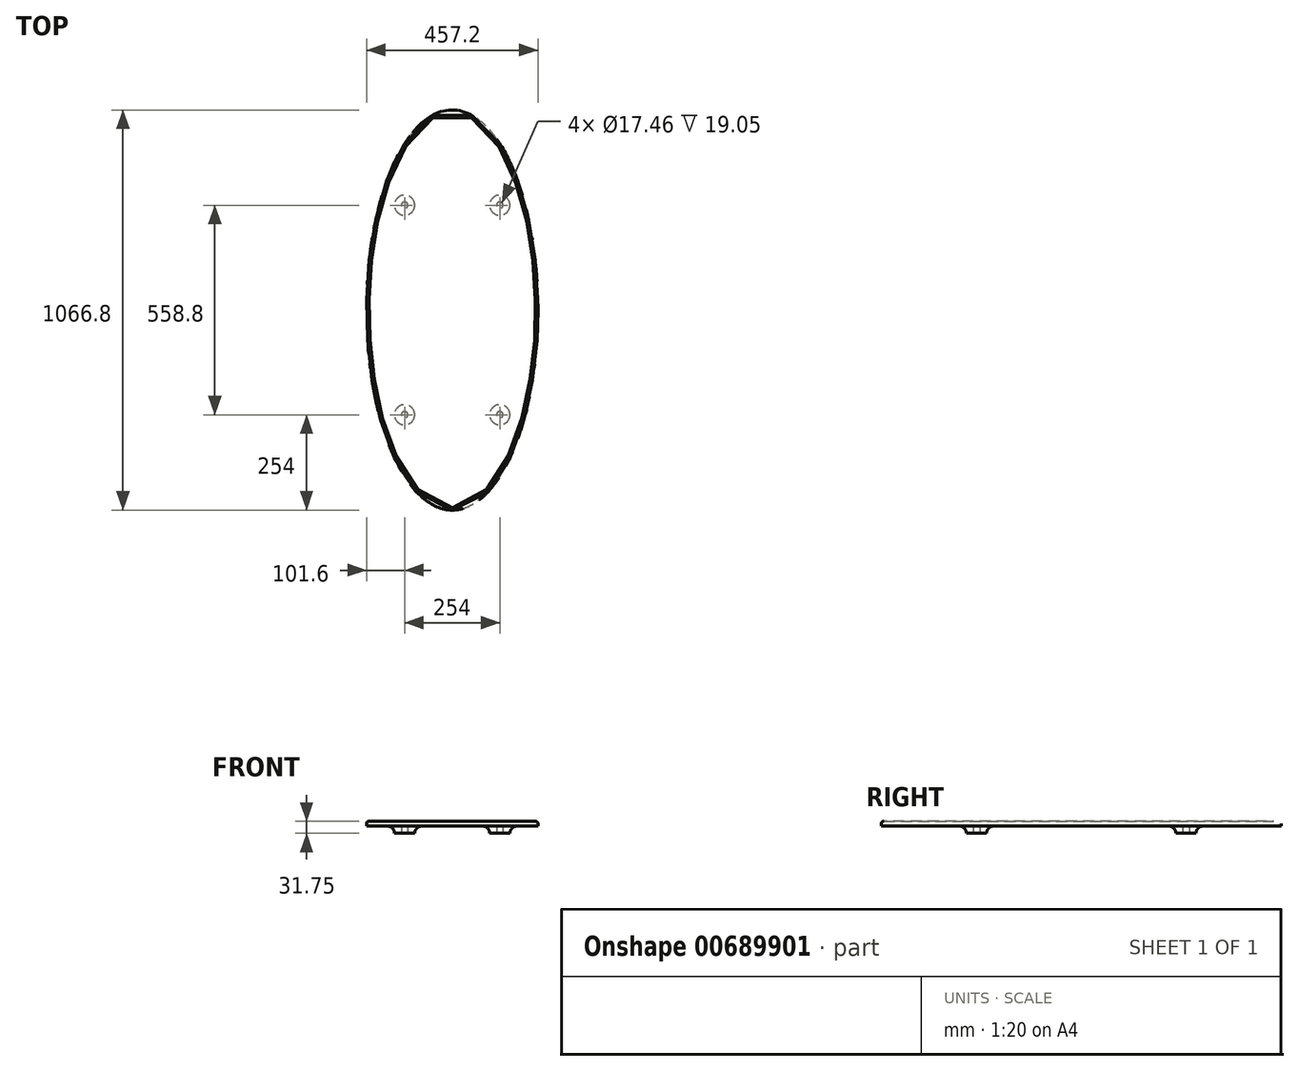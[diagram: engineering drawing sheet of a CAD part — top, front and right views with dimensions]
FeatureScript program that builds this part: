
annotation { "Feature Type Name" : "Feature", "Feature Type Description" : "" }
export const myFeature = defineFeature(function(context is Context, id is Id, definition is map)
    precondition{}
    {
        {
            var Q0;
            Q0=qCreatedBy(makeId("Top.planeOp"),FACE);
            var sketch = newSketch(context, id + "F0", { "sketchPlane" : qUnion([Q0])});
            skEllipse(sketch, "E0", {"center": v(0, 0) * mm, "majorRadius": 533.4 * mm, "minorRadius": 228.6 * mm, "majorAxis": v(0, -1)});
            skSolve(sketch);
        }
        {
            var Q0;
            Q0=makeQuery(id+"F0.imprint","IMPRINT",FACE,{"disambiguationData":[TD([[makeQuery(id+"F0.imprint","IMPRINT",EDGE,{"derivedFrom":sQuery(id+"F0.wireOp",EDGE,"E0")}),1.0]])]});
            extrude(context, id + "F1", {"entities" : qUnion([Q0]), "depth" : 31.75 * mm, "offsetDistance" : 25.4 * mm});
        }
        {
            var Q0;
            Q0=makeQuery(id+"F1.opExtrude","CAP_FACE",FACE,{"disambiguationData":[OSD([sQuery(id+"F0.wireOp",EDGE,"E0")])],"isStart":true});
            var sketch = newSketch(context, id + "F2", { "sketchPlane" : qUnion([Q0])});
            skLineSegment(sketch, "E1.bottom", {"start": v(-127, 279.4) * mm, "end": v(127, 279.4) * mm});
            skLineSegment(sketch, "E1.top", {"start": v(-127, -279.4) * mm, "end": v(127, -279.4) * mm});
            skLineSegment(sketch, "E1.left", {"start": v(-127, 279.4) * mm, "end": v(-127, -279.4) * mm});
            skLineSegment(sketch, "E1.right", {"start": v(127, 279.4) * mm, "end": v(127, -279.4) * mm});
            skPoint(sketch, "E1.middle", {"position": v(0, 0) * mm});
            skCircle(sketch, "E2", {"center": v(127, 279.4) * mm, "radius": 26.99 * mm});
            skCircle(sketch, "E3", {"center": v(-127, 279.4) * mm, "radius": 26.99 * mm});
            skCircle(sketch, "E4", {"center": v(-127, -279.4) * mm, "radius": 26.99 * mm});
            skCircle(sketch, "E5", {"center": v(127, -279.4) * mm, "radius": 26.99 * mm});
            skSolve(sketch);
        }
        {
            var Q0;
            Q0=makeQuery(id+"F2.imprint","IMPRINT",FACE,{"disambiguationData":[TD([[makeQuery(id+"F2.imprint","IMPRINT",EDGE,{"derivedFrom":makeQuery(id+"F1.opExtrude","CAP_EDGE",EDGE,{"disambiguationData":[OSD([sQuery(id+"F0.wireOp",EDGE,"E0")])],"isStart":true})}),-1.0]])]});
            var Q1;
            {var subQ5=sQuery(id+"F2.wireOp",EDGE,"E3");var subQ13=sQuery(id+"F2.wireOp",EDGE,"E1.bottom");var subQ14=makeQuery(id+"F2.imprint","INTERSECT",VERTEX,{"derivedFrom":[subQ13,subQ5]});Q1=makeQuery(id+"F2.imprint","IMPRINT",FACE,{"disambiguationData":[TD([[makeQuery(id+"F2.imprint","IMPRINT",EDGE,{"disambiguationData":[TD([[subQ14,-1.0]])],"derivedFrom":subQ13}),-1.0]])]});}
            extrude(context, id + "F3", {"entities" : qUnion([Q0, Q1]), "operationType" : NewBodyOperationType.REMOVE, "oppositeDirection" : true, "depth" : 19.05 * mm, "offsetDistance" : 25.4 * mm});
        }
        {
            var Q0;
            Q0=makeQuery(id+"F3.boolean.opBoolean","COPY",EDGE,{"derivedFrom":makeQuery(id+"F3.opExtrude","CAP_EDGE",EDGE,{"disambiguationData":[OSD([sQuery(id+"F2.wireOp",EDGE,"E2")])],"isStart":false})});
            var Q1;
            Q1=makeQuery(id+"F3.boolean.opBoolean","COPY",EDGE,{"derivedFrom":makeQuery(id+"F3.opExtrude","CAP_EDGE",EDGE,{"disambiguationData":[OSD([sQuery(id+"F2.wireOp",EDGE,"E3")])],"isStart":false})});
            var Q2;
            Q2=makeQuery(id+"F3.boolean.opBoolean","COPY",EDGE,{"derivedFrom":makeQuery(id+"F3.opExtrude","CAP_EDGE",EDGE,{"disambiguationData":[OSD([sQuery(id+"F2.wireOp",EDGE,"E5")])],"isStart":false})});
            var Q3;
            Q3=makeQuery(id+"F3.boolean.opBoolean","COPY",EDGE,{"derivedFrom":makeQuery(id+"F3.opExtrude","CAP_EDGE",EDGE,{"disambiguationData":[OSD([sQuery(id+"F2.wireOp",EDGE,"E4")])],"isStart":false})});
            fillet(context, id + "F4", {"entities" : qUnion([Q0, Q1, Q2, Q3]), "radius" : 19.05 * mm, "tangentPropagation" : true, "allowEdgeOverflow" : false});
        }
        {
            var Q0;
            Q0=makeQuery(id+"F1.opExtrude","CAP_EDGE",EDGE,{"disambiguationData":[OSD([sQuery(id+"F0.wireOp",EDGE,"E0")])],"isStart":false});
            var Q1;
            Q1=makeQuery(id+"F3.boolean.opBoolean","COPY",EDGE,{"derivedFrom":makeQuery(id+"F3.opExtrude","CAP_EDGE",EDGE,{"disambiguationData":[OSD([sQuery(id+"F0.wireOp",EDGE,"E0")])],"isStart":false})});
            fillet(context, id + "F5", {"entities" : qUnion([Q0, Q1]), "radius" : 6.35 * mm, "tangentPropagation" : true, "allowEdgeOverflow" : false});
        }
        {
            var Q0;
            Q0=makeQuery(id+"F3.boolean.opBoolean","SPLIT",FACE,{"disambiguationData":[TD([makeQuery(id+"F3.opExtrude","SWEPT_FACE",FACE,{"disambiguationData":[OSD([sQuery(id+"F2.wireOp",EDGE,"E4")])]})])],"derivedFrom":makeQuery(id+"F1.opExtrude","CAP_FACE",FACE,{"disambiguationData":[OSD([sQuery(id+"F0.wireOp",EDGE,"E0")])],"isStart":true})});
            var sketch = newSketch(context, id + "F6", { "sketchPlane" : qUnion([Q0])});
            skCircle(sketch, "E6", {"center": v(-127, -279.4) * mm, "radius": 8.73 * mm});
            skSolve(sketch);
        }
        {
            var Q0;
            Q0=makeQuery(id+"F3.boolean.opBoolean","SPLIT",FACE,{"disambiguationData":[TD([makeQuery(id+"F3.opExtrude","SWEPT_FACE",FACE,{"disambiguationData":[OSD([sQuery(id+"F2.wireOp",EDGE,"E3")])]})])],"derivedFrom":makeQuery(id+"F1.opExtrude","CAP_FACE",FACE,{"disambiguationData":[OSD([sQuery(id+"F0.wireOp",EDGE,"E0")])],"isStart":true})});
            var sketch = newSketch(context, id + "F7", { "sketchPlane" : qUnion([Q0])});
            skCircle(sketch, "E7", {"center": v(-127, 279.4) * mm, "radius": 8.73 * mm});
            skSolve(sketch);
        }
        {
            var Q0;
            Q0=makeQuery(id+"F3.boolean.opBoolean","SPLIT",FACE,{"disambiguationData":[TD([makeQuery(id+"F3.opExtrude","SWEPT_FACE",FACE,{"disambiguationData":[OSD([sQuery(id+"F2.wireOp",EDGE,"E5")])]})])],"derivedFrom":makeQuery(id+"F1.opExtrude","CAP_FACE",FACE,{"disambiguationData":[OSD([sQuery(id+"F0.wireOp",EDGE,"E0")])],"isStart":true})});
            var sketch = newSketch(context, id + "F8", { "sketchPlane" : qUnion([Q0])});
            skCircle(sketch, "E8", {"center": v(127, -279.4) * mm, "radius": 8.73 * mm});
            skSolve(sketch);
        }
        {
            var Q0;
            Q0=makeQuery(id+"F3.boolean.opBoolean","SPLIT",FACE,{"disambiguationData":[TD([makeQuery(id+"F3.opExtrude","SWEPT_FACE",FACE,{"disambiguationData":[OSD([sQuery(id+"F2.wireOp",EDGE,"E2")])]})])],"derivedFrom":makeQuery(id+"F1.opExtrude","CAP_FACE",FACE,{"disambiguationData":[OSD([sQuery(id+"F0.wireOp",EDGE,"E0")])],"isStart":true})});
            var sketch = newSketch(context, id + "F9", { "sketchPlane" : qUnion([Q0])});
            skCircle(sketch, "E9", {"center": v(127, 279.4) * mm, "radius": 8.73 * mm});
            skSolve(sketch);
        }
        {
            var Q0;
            Q0=makeQuery(id+"F6.imprint","IMPRINT",FACE,{"disambiguationData":[TD([[makeQuery(id+"F6.imprint","IMPRINT",EDGE,{"derivedFrom":sQuery(id+"F6.wireOp",EDGE,"E6")}),1.0]])]});
            var Q1;
            Q1=makeQuery(id+"F7.imprint","IMPRINT",FACE,{"disambiguationData":[TD([[makeQuery(id+"F7.imprint","IMPRINT",EDGE,{"derivedFrom":sQuery(id+"F7.wireOp",EDGE,"E7")}),1.0]])]});
            var Q2;
            Q2=makeQuery(id+"F9.imprint","IMPRINT",FACE,{"disambiguationData":[TD([[makeQuery(id+"F9.imprint","IMPRINT",EDGE,{"derivedFrom":sQuery(id+"F9.wireOp",EDGE,"E9")}),1.0]])]});
            var Q3;
            Q3=makeQuery(id+"F8.imprint","IMPRINT",FACE,{"disambiguationData":[TD([[makeQuery(id+"F8.imprint","IMPRINT",EDGE,{"derivedFrom":sQuery(id+"F8.wireOp",EDGE,"E8")}),1.0]])]});
            extrude(context, id + "F10", {"entities" : qUnion([Q0, Q1, Q2, Q3]), "operationType" : NewBodyOperationType.REMOVE, "oppositeDirection" : true, "depth" : 19.05 * mm, "offsetDistance" : 25.4 * mm});
        }
    });
